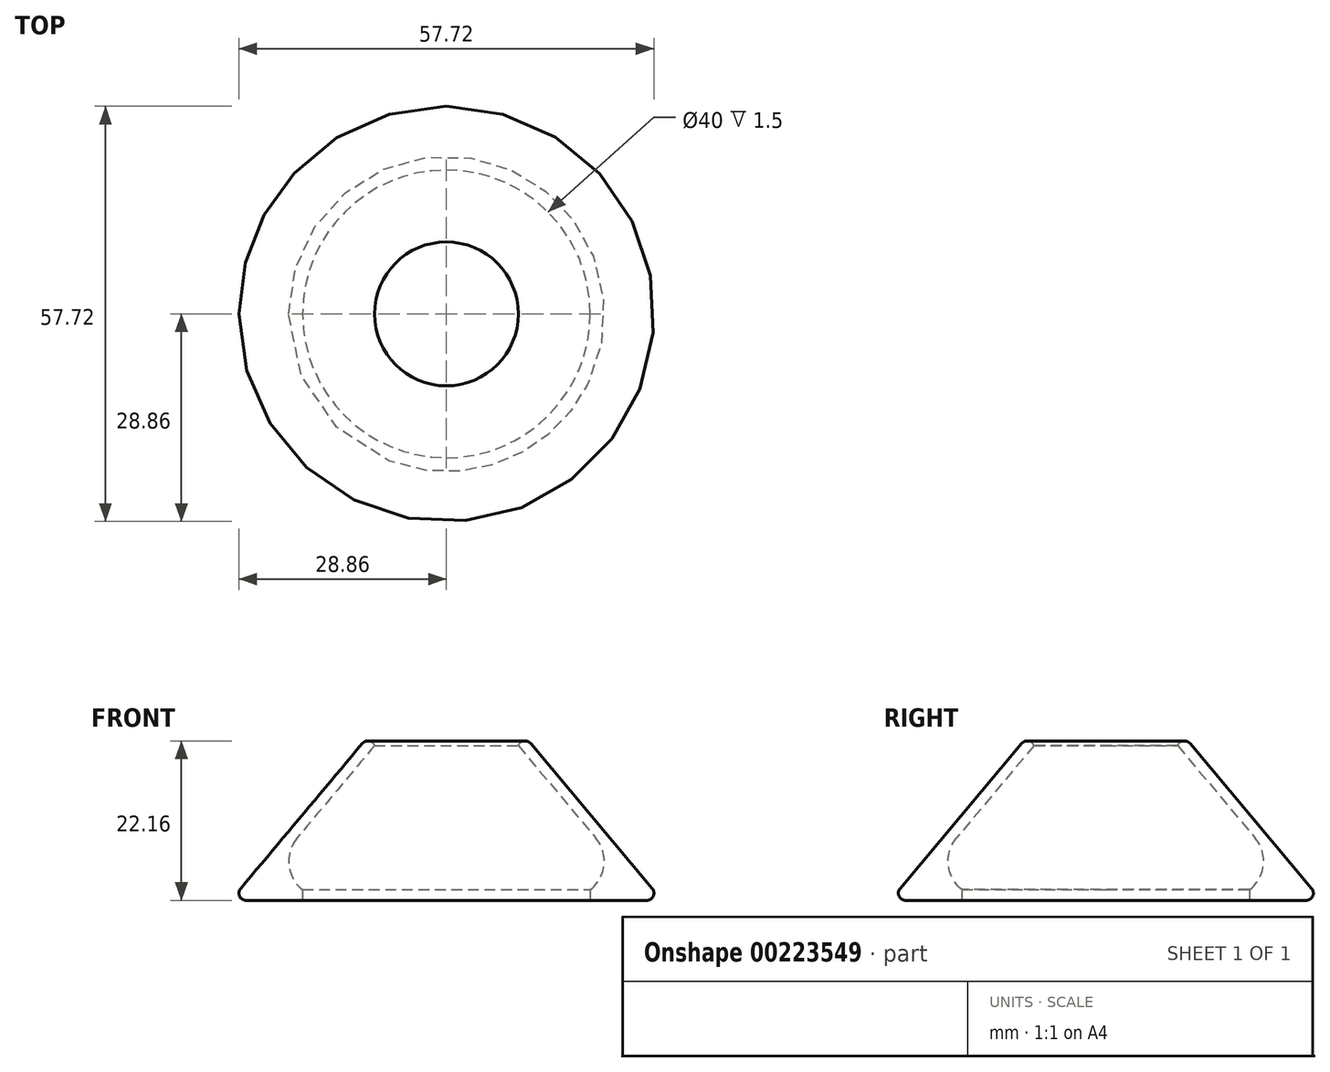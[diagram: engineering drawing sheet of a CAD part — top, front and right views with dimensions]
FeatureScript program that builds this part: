
annotation { "Feature Type Name" : "Feature", "Feature Type Description" : "" }
export const myFeature = defineFeature(function(context is Context, id is Id, definition is map)
    precondition{}
    {
        {
            var Q0;
            Q0=qCreatedBy(makeId("Front.planeOp"),FACE);
            var sketch = newSketch(context, id + "F0", { "sketchPlane" : qUnion([Q0])});
            skLineSegment(sketch, "E0", {"start": v(20, 0) * mm, "end": v(30, 0) * mm});
            skLineSegment(sketch, "E1", {"start": v(30, 0) * mm, "end": v(10, 23.84) * mm});
            skLineSegment(sketch, "E2", {"start": v(10, 21.5) * mm, "end": v(26.78, 1.5) * mm});
            skLineSegment(sketch, "E3", {"start": v(26.78, 1.5) * mm, "end": v(20, 1.5) * mm});
            skLineSegment(sketch, "E4", {"start": v(20, 1.5) * mm, "end": v(20, 0) * mm});
            skLineSegment(sketch, "E5", {"start": v(10, 23.84) * mm, "end": v(10, 21.5) * mm});
            skLineSegment(sketch, "E6", {"start": v(0, 0) * mm, "end": v(0, 24.25) * mm, "construction": true});
            skSolve(sketch);
        }
        {
            var Q0;
            Q0 = qSketchRegion(id + "F0", true);
            var Q1;
            Q1=sQuery(id+"F0.wireOp",EDGE,"E6");
            revolve(context, id + "F1", {"entities" : qUnion([Q0]), "axis" : qUnion([Q1]), "revolveType" : RevolveType.FULL});
        }
        {
            var Q0;
            Q0=makeQuery(id+"F1.opRevolve","SWEPT_EDGE",EDGE,{"disambiguationData":[OSD([sQuery(id+"F0.wireOp",EDGE,"E2"),sQuery(id+"F0.wireOp",EDGE,"E3")])]});
            fillet(context, id + "F2", {"entities" : qUnion([Q0]), "radius" : 5 * mm, "tangentPropagation" : true, "allowEdgeOverflow" : false});
        }
        {
            var Q0;
            Q0=makeQuery(id+"F1.opRevolve","SWEPT_EDGE",EDGE,{"disambiguationData":[OSD([sQuery(id+"F0.wireOp",EDGE,"E0"),sQuery(id+"F0.wireOp",EDGE,"E1")])]});
            var Q1;
            Q1=makeQuery(id+"F1.opRevolve","SWEPT_EDGE",EDGE,{"disambiguationData":[OSD([sQuery(id+"F0.wireOp",EDGE,"E1"),sQuery(id+"F0.wireOp",EDGE,"E5")])]});
            fillet(context, id + "F3", {"entities" : qUnion([Q0, Q1]), "radius" : 1 * mm, "tangentPropagation" : true, "allowEdgeOverflow" : false});
        }
    });
